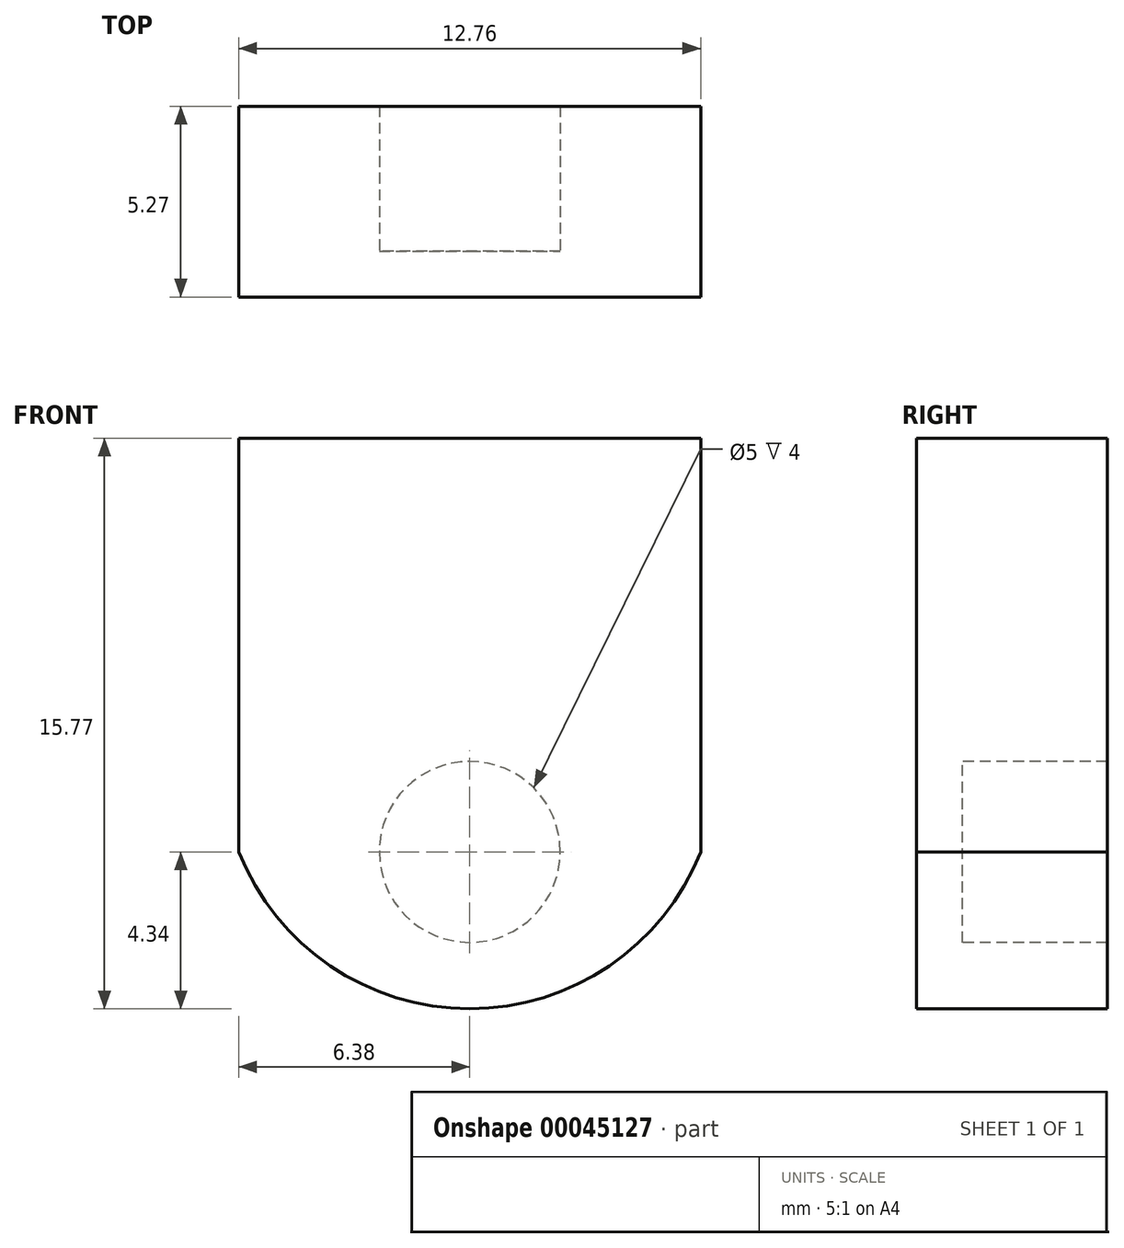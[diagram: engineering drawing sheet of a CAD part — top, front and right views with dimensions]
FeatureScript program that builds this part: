
annotation { "Feature Type Name" : "Feature", "Feature Type Description" : "" }
export const myFeature = defineFeature(function(context is Context, id is Id, definition is map)
    precondition{}
    {
        {
            var Q0;
            Q0=qCreatedBy(makeId("Front.planeOp"),FACE);
            var sketch = newSketch(context, id + "F0", { "sketchPlane" : qUnion([Q0])});
            skCircle(sketch, "E0", {"center": v(0, 0) * mm, "radius": 2.5 * mm});
            skLineSegment(sketch, "E1", {"start": v(-6.38, 0) * mm, "end": v(-6.38, 11.43) * mm});
            skLineSegment(sketch, "E2", {"start": v(6.38, 0) * mm, "end": v(6.38, 11.43) * mm});
            skLineSegment(sketch, "E3", {"start": v(-6.38, 11.43) * mm, "end": v(6.38, 11.43) * mm});
            skArc(sketch, "E4", {"start": v(-6.38, 0) * mm, "mid": v(0, -4.34) * mm, "end": v(6.38, 0) * mm});
            skSolve(sketch);
        }
        {
            var Q0;
            Q0 = qSketchRegion(id + "F0", true);
            extrude(context, id + "F1", {"entities" : qUnion([Q0]), "oppositeDirection" : true, "depth" : 4 * mm});
        }
        {
            var Q0;
            Q0=makeQuery(id+"F0.imprint","IMPRINT",FACE,{"disambiguationData":[TD([[makeQuery(id+"F0.imprint","IMPRINT",EDGE,{"derivedFrom":sQuery(id+"F0.wireOp",EDGE,"E0")}),-1.0]])]});
            var Q1;
            Q1=makeQuery(id+"F0.imprint","IMPRINT",FACE,{"disambiguationData":[TD([[makeQuery(id+"F0.imprint","IMPRINT",EDGE,{"derivedFrom":sQuery(id+"F0.wireOp",EDGE,"E0")}),1.0]])]});
            extrude(context, id + "F2", {"entities" : qUnion([Q0, Q1]), "operationType" : NewBodyOperationType.ADD, "depth" : 1.27 * mm});
        }
    });
